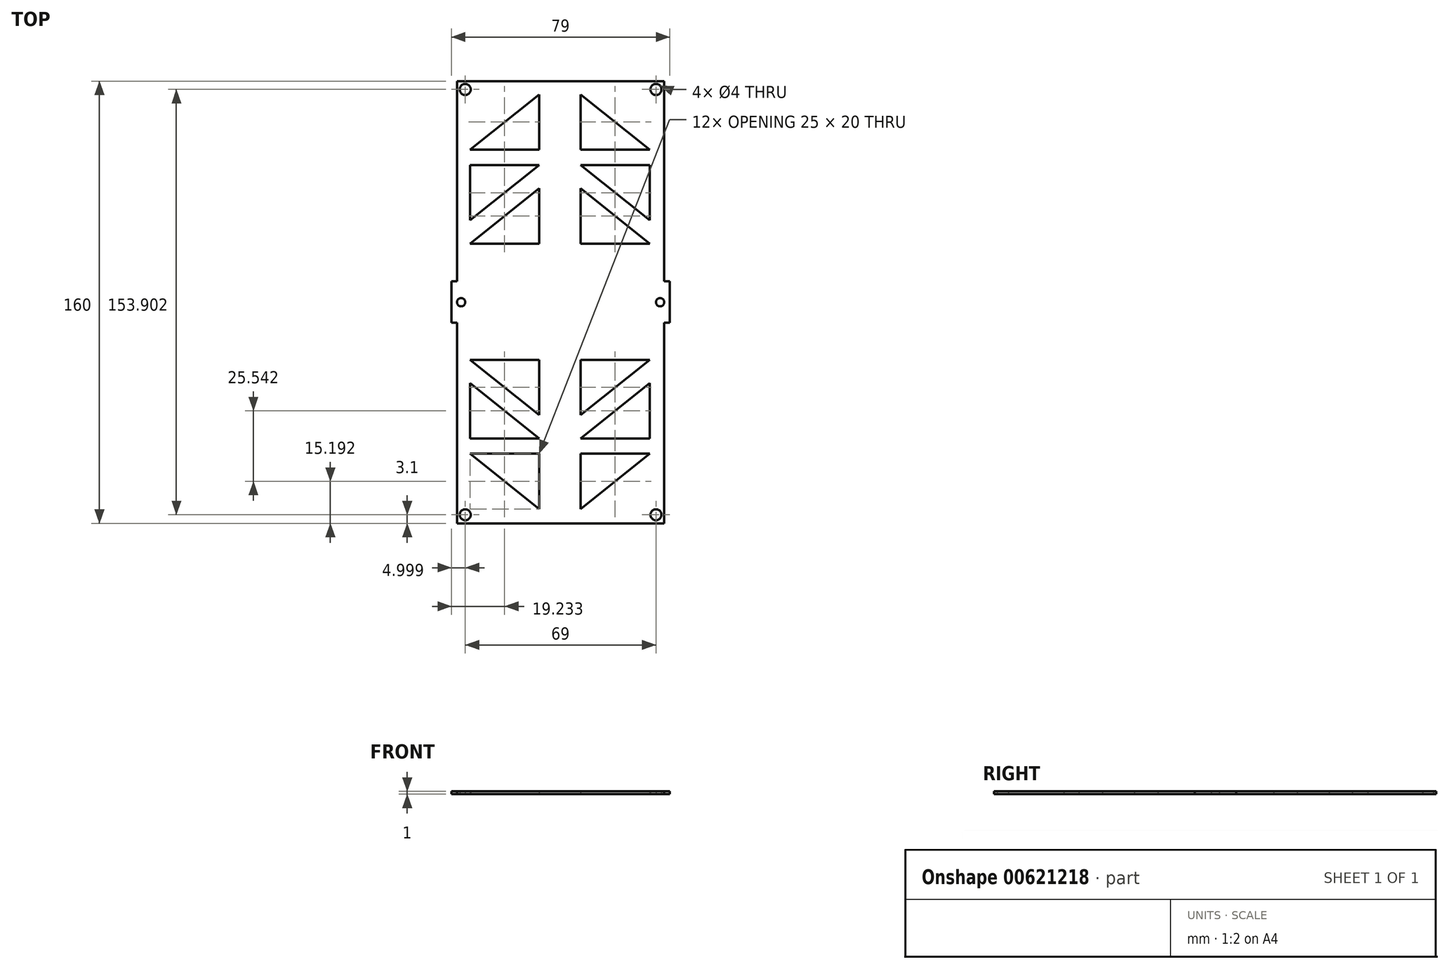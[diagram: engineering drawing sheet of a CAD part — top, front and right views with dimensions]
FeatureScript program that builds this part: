
annotation { "Feature Type Name" : "Feature", "Feature Type Description" : "" }
export const myFeature = defineFeature(function(context is Context, id is Id, definition is map)
    precondition{}
    {
        {
            var Q0;
            Q0=qCreatedBy(makeId("Top.planeOp"),FACE);
            var sketch = newSketch(context, id + "F0", { "sketchPlane" : qUnion([Q0])});
            skLineSegment(sketch, "E0.bottom", {"start": v(-38.08, 80.58) * mm, "end": v(36.92, 80.58) * mm});
            skLineSegment(sketch, "E0.top", {"start": v(-38.08, -79.42) * mm, "end": v(36.92, -79.42) * mm});
            skLineSegment(sketch, "E0.left", {"start": v(-38.08, 80.58) * mm, "end": v(-38.08, -79.42) * mm});
            skLineSegment(sketch, "E0.right", {"start": v(36.92, 80.58) * mm, "end": v(36.92, -79.42) * mm});
            skPoint(sketch, "E0.middle", {"position": v(-0.58, 0.58) * mm});
            skLineSegment(sketch, "E1.bottom", {"start": v(-38.08, -19.37) * mm, "end": v(-40.08, -19.37) * mm});
            skLineSegment(sketch, "E1.top", {"start": v(-38.08, 20.63) * mm, "end": v(-40.08, 20.63) * mm});
            skLineSegment(sketch, "E1.left", {"start": v(-38.08, -19.37) * mm, "end": v(-38.08, 20.63) * mm});
            skLineSegment(sketch, "E1.right", {"start": v(-40.08, -19.37) * mm, "end": v(-40.08, 20.63) * mm});
            skLineSegment(sketch, "E2.MirrorCS", {"start": v(38.92, -14.43) * mm, "end": v(38.92, 15.57) * mm});
            skLineSegment(sketch, "E3.MirrorCS", {"start": v(36.92, -14.43) * mm, "end": v(38.92, -14.43) * mm});
            skLineSegment(sketch, "E4.MirrorCS", {"start": v(36.92, 15.57) * mm, "end": v(38.92, 15.57) * mm});
            skLineSegment(sketch, "E5", {"start": v(-33.35, 55.77) * mm, "end": v(-8.35, 75.77) * mm});
            skLineSegment(sketch, "E6", {"start": v(-8.35, 55.77) * mm, "end": v(-8.35, 75.77) * mm});
            skLineSegment(sketch, "E7", {"start": v(-8.35, 55.77) * mm, "end": v(-33.35, 55.77) * mm});
            skLineSegment(sketch, "E8.MirrorCS", {"start": v(6.65, 55.77) * mm, "end": v(31.65, 55.77) * mm});
            skLineSegment(sketch, "E9.MirrorCS", {"start": v(31.65, 55.77) * mm, "end": v(6.65, 75.77) * mm});
            skLineSegment(sketch, "E10.MirrorCS", {"start": v(6.65, 55.77) * mm, "end": v(6.65, 75.77) * mm});
            skLineSegment(sketch, "E11.MirrorCS", {"start": v(-8.35, -54.23) * mm, "end": v(-33.35, -54.23) * mm});
            skLineSegment(sketch, "E12.MirrorCS", {"start": v(-33.35, -54.23) * mm, "end": v(-8.35, -74.23) * mm});
            skLineSegment(sketch, "E13.MirrorCS", {"start": v(-8.35, -54.23) * mm, "end": v(-8.35, -74.23) * mm});
            skLineSegment(sketch, "E14.MirrorCS", {"start": v(6.65, -54.23) * mm, "end": v(6.65, -74.23) * mm});
            skLineSegment(sketch, "E15.MirrorCS", {"start": v(6.65, -54.23) * mm, "end": v(31.65, -54.23) * mm});
            skLineSegment(sketch, "E16.MirrorCS", {"start": v(31.65, -54.23) * mm, "end": v(6.65, -74.23) * mm});
            skLineSegment(sketch, "E17.MirrorCS", {"start": v(-8.35, 21.77) * mm, "end": v(-33.35, 21.77) * mm});
            skLineSegment(sketch, "E18.MirrorCS", {"start": v(-33.35, 21.77) * mm, "end": v(-8.35, 41.77) * mm});
            skLineSegment(sketch, "E19.MirrorCS", {"start": v(-8.35, 21.77) * mm, "end": v(-8.35, 41.77) * mm});
            skLineSegment(sketch, "E20.MirrorCS", {"start": v(6.65, 21.77) * mm, "end": v(6.65, 41.77) * mm});
            skLineSegment(sketch, "E21.MirrorCS", {"start": v(31.65, 21.77) * mm, "end": v(6.65, 41.77) * mm});
            skLineSegment(sketch, "E22.MirrorCS", {"start": v(6.65, 21.77) * mm, "end": v(31.65, 21.77) * mm});
            skLineSegment(sketch, "E23.MirrorCS", {"start": v(-8.35, -20.23) * mm, "end": v(-33.35, -20.23) * mm});
            skLineSegment(sketch, "E24.MirrorCS", {"start": v(-33.35, -20.23) * mm, "end": v(-8.35, -40.23) * mm});
            skLineSegment(sketch, "E25.MirrorCS", {"start": v(6.65, -20.23) * mm, "end": v(6.65, -40.23) * mm});
            skLineSegment(sketch, "E26.MirrorCS", {"start": v(31.65, -20.23) * mm, "end": v(6.65, -40.23) * mm});
            skLineSegment(sketch, "E27.MirrorCS", {"start": v(6.65, -20.23) * mm, "end": v(31.65, -20.23) * mm});
            skLineSegment(sketch, "E28.MirrorCS", {"start": v(-8.35, -20.23) * mm, "end": v(-8.35, -40.23) * mm});
            skLineSegment(sketch, "E29", {"start": v(-33.35, 30.23) * mm, "end": v(-8.35, 50.23) * mm});
            skLineSegment(sketch, "E30", {"start": v(-8.35, 50.23) * mm, "end": v(-33.35, 50.23) * mm});
            skLineSegment(sketch, "E31", {"start": v(-33.35, 50.23) * mm, "end": v(-33.35, 30.23) * mm});
            skLineSegment(sketch, "E32.MirrorCS", {"start": v(31.65, 30.23) * mm, "end": v(6.65, 50.23) * mm});
            skLineSegment(sketch, "E33.MirrorCS", {"start": v(6.65, 50.23) * mm, "end": v(31.65, 50.23) * mm});
            skLineSegment(sketch, "E34.MirrorCS", {"start": v(31.65, 50.23) * mm, "end": v(31.65, 30.23) * mm});
            skLineSegment(sketch, "E35.MirrorCS", {"start": v(-33.35, -28.69) * mm, "end": v(-8.35, -48.69) * mm});
            skLineSegment(sketch, "E36.MirrorCS", {"start": v(-33.35, -48.69) * mm, "end": v(-33.35, -28.69) * mm});
            skLineSegment(sketch, "E37.MirrorCS", {"start": v(-8.35, -48.69) * mm, "end": v(-33.35, -48.69) * mm});
            skLineSegment(sketch, "E38.MirrorCS", {"start": v(6.65, -48.69) * mm, "end": v(31.65, -48.69) * mm});
            skLineSegment(sketch, "E39.MirrorCS", {"start": v(31.65, -28.69) * mm, "end": v(6.65, -48.69) * mm});
            skLineSegment(sketch, "E40.MirrorCS", {"start": v(31.65, -48.69) * mm, "end": v(31.65, -28.69) * mm});
            skLineSegment(sketch, "E41.MirrorCS", {"start": v(38.92, -19.37) * mm, "end": v(38.92, 20.63) * mm});
            skLineSegment(sketch, "E42.MirrorCS", {"start": v(36.92, 20.63) * mm, "end": v(38.92, 20.63) * mm});
            skLineSegment(sketch, "E43.MirrorCS", {"start": v(36.92, -19.37) * mm, "end": v(38.92, -19.37) * mm});
            skLineSegment(sketch, "E44.MirrorCS", {"start": v(-38.08, -14.43) * mm, "end": v(-40.08, -14.43) * mm});
            skLineSegment(sketch, "E45.MirrorCS", {"start": v(-38.08, 15.57) * mm, "end": v(-40.08, 15.57) * mm});
            skLineSegment(sketch, "E46.bottom", {"start": v(-38.08, 8.13) * mm, "end": v(-40.08, 8.13) * mm});
            skLineSegment(sketch, "E46.top", {"start": v(-38.08, -6.87) * mm, "end": v(-40.08, -6.87) * mm});
            skLineSegment(sketch, "E46.left", {"start": v(-38.08, 8.13) * mm, "end": v(-38.08, -6.87) * mm});
            skLineSegment(sketch, "E46.right", {"start": v(-40.08, 8.13) * mm, "end": v(-40.08, -6.87) * mm});
            skLineSegment(sketch, "E47.MirrorCS", {"start": v(36.92, 8.13) * mm, "end": v(38.92, 8.13) * mm});
            skLineSegment(sketch, "E48.MirrorCS", {"start": v(36.92, -6.87) * mm, "end": v(38.92, -6.87) * mm});
            skLineSegment(sketch, "E49.bottom", {"start": v(-40.08, 20.63) * mm, "end": v(-43.08, 20.63) * mm});
            skLineSegment(sketch, "E49.top", {"start": v(-40.08, -19.37) * mm, "end": v(-43.08, -19.37) * mm});
            skLineSegment(sketch, "E49.left", {"start": v(-40.08, 20.63) * mm, "end": v(-40.08, -19.37) * mm});
            skLineSegment(sketch, "E49.right", {"start": v(-43.08, 20.63) * mm, "end": v(-43.08, -19.37) * mm});
            skLineSegment(sketch, "E50.MirrorCS", {"start": v(-46.08, 20.63) * mm, "end": v(-43.08, 20.63) * mm});
            skLineSegment(sketch, "E51.MirrorCS", {"start": v(41.92, 20.63) * mm, "end": v(41.92, -19.37) * mm});
            skLineSegment(sketch, "E52.MirrorCS", {"start": v(38.92, 20.63) * mm, "end": v(41.92, 20.63) * mm});
            skLineSegment(sketch, "E53.MirrorCS", {"start": v(38.92, -19.37) * mm, "end": v(41.92, -19.37) * mm});
            skCircle(sketch, "E54", {"center": v(-35.08, 77.58) * mm, "radius": 2 * mm});
            skCircle(sketch, "E55.MirrorC", {"center": v(33.92, 77.58) * mm, "radius": 2 * mm});
            skCircle(sketch, "E56.MirrorC", {"center": v(-35.08, -76.32) * mm, "radius": 2 * mm});
            skCircle(sketch, "E57.MirrorC", {"center": v(33.92, -76.32) * mm, "radius": 2 * mm});
            skLineSegment(sketch, "E58.bottom", {"start": v(-40.08, 5.63) * mm, "end": v(-43.08, 5.63) * mm});
            skLineSegment(sketch, "E58.top", {"start": v(-40.08, -4.37) * mm, "end": v(-43.08, -4.37) * mm});
            skLineSegment(sketch, "E58.left", {"start": v(-40.08, 5.63) * mm, "end": v(-40.08, -4.37) * mm});
            skLineSegment(sketch, "E58.right", {"start": v(-43.08, 5.63) * mm, "end": v(-43.08, -4.37) * mm});
            skLineSegment(sketch, "E59.MirrorCS", {"start": v(38.92, 5.63) * mm, "end": v(41.92, 5.63) * mm});
            skLineSegment(sketch, "E60.MirrorCS", {"start": v(38.92, -4.37) * mm, "end": v(41.92, -4.37) * mm});
            skCircle(sketch, "E61", {"center": v(35.42, 0.58) * mm, "radius": 1.5 * mm});
            skPoint(sketch, "E61.centerSnap0", {"position": v(36.92, 0.58) * mm});
            skCircle(sketch, "E62", {"center": v(-36.58, 0.58) * mm, "radius": 1.5 * mm});
            skSolve(sketch);
        }
        {
            var Q0;
            {var subQ9=sQuery(id+"F0.wireOp",EDGE,"E0.bottom");Q0=makeQuery(id+"F0.imprint","IMPRINT",FACE,{"disambiguationData":[TD([[makeQuery(id+"F0.imprint","IMPRINT",EDGE,{"derivedFrom":subQ9}),-1.0]])]});}
            var Q1;
            {var subQ7=sQuery(id+"F0.wireOp",EDGE,"E47.MirrorCS");Q1=makeQuery(id+"F0.imprint","IMPRINT",FACE,{"disambiguationData":[TD([[makeQuery(id+"F0.imprint","IMPRINT",EDGE,{"derivedFrom":subQ7}),-1.0]])]});}
            var Q2;
            {var subQ5=sQuery(id+"F0.wireOp",EDGE,"E46.bottom");Q2=makeQuery(id+"F0.imprint","IMPRINT",FACE,{"disambiguationData":[TD([[makeQuery(id+"F0.imprint","IMPRINT",EDGE,{"derivedFrom":subQ5}),1.0]])]});}
            extrude(context, id + "F1", {"entities" : qUnion([Q0, Q1, Q2]), "depth" : 1 * mm, "offsetDistance" : 25 * mm});
        }
    });
